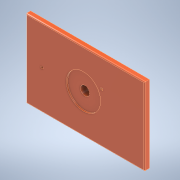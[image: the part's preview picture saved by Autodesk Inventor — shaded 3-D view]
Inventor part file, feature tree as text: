
AUTODESK INVENTOR PART (.ipt)
format: ipt  version: 2022.2 (Build 262287010, 287A)  size: 187,392 bytes
history: native  units: mm
features: extrude x8, sketch x7, fillet x2, other x1
ambient origin geometry x8: Origin, YZ Plane, XZ Plane, XY Plane, X Axis, Y Axis, Z Axis, Center Point
bodies: Body1 (feature_tree)
feature tree (18):
  other  "Sólido1"
  extrude  "Extrusión1"  Depth=170.0mm
  extrude  "Extrusión2"  Depth=5.0mm
  extrude  "Extrusión4"  TaperAngle=0.0deg  [1 undecoded]
  fillet  "Empalme1"  Radius=85.0mm
  fillet  "Empalme2"  Radius=10.5mm
  extrude  "Extrusión5"  Depth=5.0mm
  extrude  "Extrusión6"  Depth=10.0mm
  extrude  "Extrusión7"  Depth=35.0mm
  extrude  "Extrusión8"  Depth=2.0mm
  extrude  "Extrusión9"  Depth=2.0mm
  sketch  "Boceto2"  dims[d0=260.0mm d1=170.0mm]
  sketch  "Boceto5"  dims[d2=10.0mm d3=0.0mm d7=5.0mm]
  sketch  "Boceto6"  dims[d8=20.0mm d9=0.0mm d10=0.0mm d14=85.0mm d23=10.5mm]
  sketch  "Boceto8"  dims[d24=40.0mm d25=5.0mm]
  sketch  "Boceto9"  dims[d26=10.0mm d27=0.0mm d29=50.0mm]
  sketch  "Boceto10"  dims[d30=90.81mm d31=35.0mm]
  sketch  "Boceto11"  dims[d32=134.19mm d33=2.0mm d34=2.0mm d35=40.0mm d36=25.0mm d38=4.0mm d39=3.0mm d40=1.4mm d41=0.0mm d42=4.0mm d43=1.0mm d44=2.0mm d45=0.0mm d47=75.0mm d48=3.0mm d49=0.0mm d50=37.0mm d51=12.0mm d52=10.0mm d53=0.0mm d54=12.0mm d55=5.0mm d56=0.0mm d46=0.5mm]
note: 1 required parameter value undecoded (feature->parameter linkage not recoverable at this tier; creation-order binding heuristic only, values carry confidence <= 0.55)
